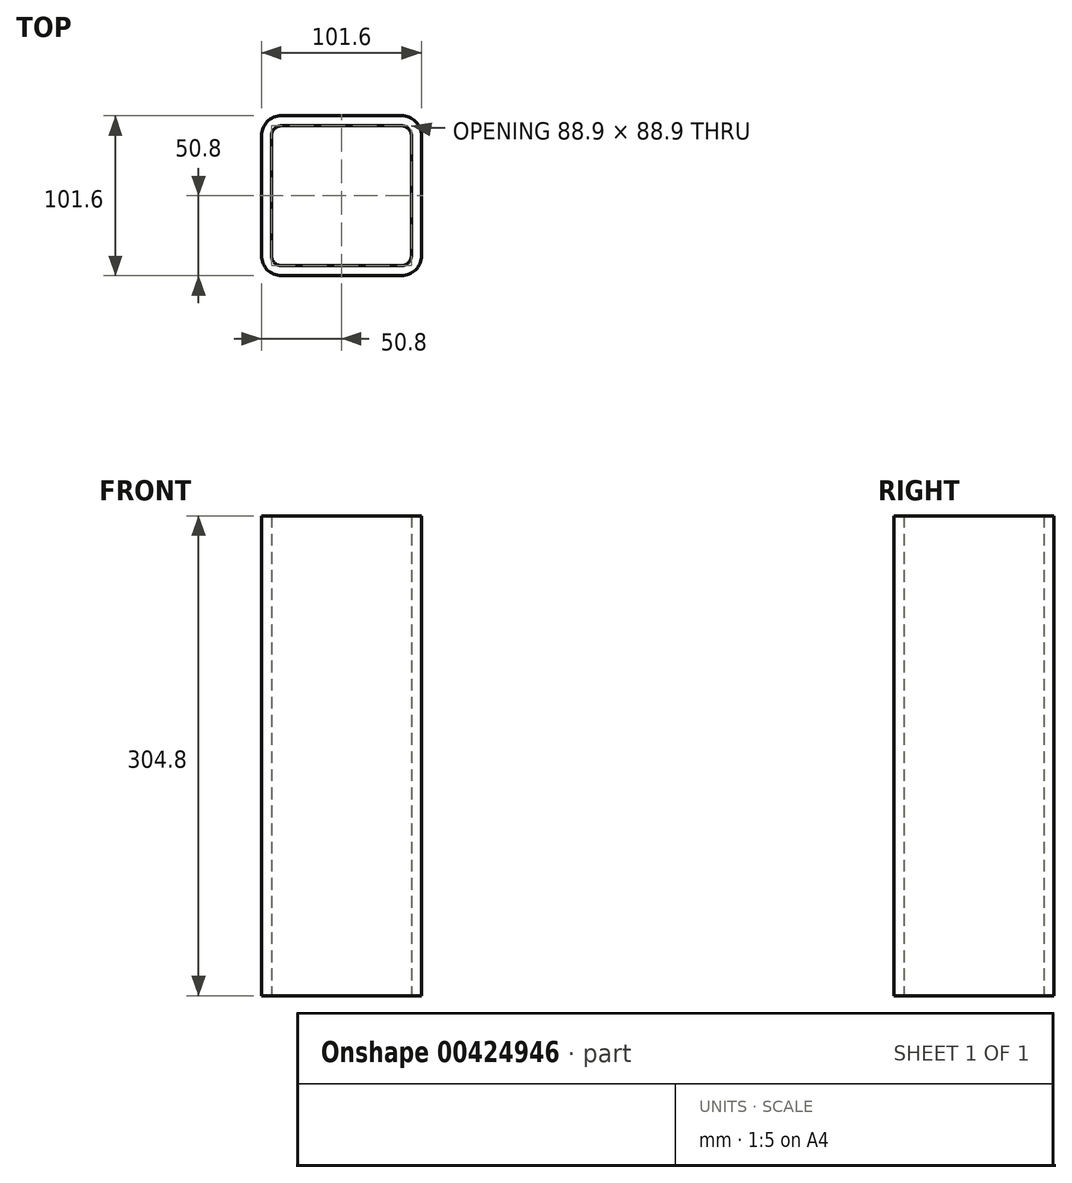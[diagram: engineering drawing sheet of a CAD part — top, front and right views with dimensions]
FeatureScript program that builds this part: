
annotation { "Feature Type Name" : "Feature", "Feature Type Description" : "" }
export const myFeature = defineFeature(function(context is Context, id is Id, definition is map)
    precondition{}
    {
        {
            var Q0;
            Q0=qCreatedBy(makeId("Top.planeOp"),FACE);
            var sketch = newSketch(context, id + "F0", { "sketchPlane" : qUnion([Q0])});
            skLineSegment(sketch, "E0.bottom", {"start": v(38.1, -50.8) * mm, "end": v(-38.1, -50.8) * mm});
            skLineSegment(sketch, "E0.top", {"start": v(38.1, 50.8) * mm, "end": v(-38.1, 50.8) * mm});
            skLineSegment(sketch, "E0.left", {"start": v(50.8, -38.1) * mm, "end": v(50.8, 38.1) * mm});
            skLineSegment(sketch, "E0.right", {"start": v(-50.8, -38.1) * mm, "end": v(-50.8, 38.1) * mm});
            skPoint(sketch, "E0.middle", {"position": v(0, 0) * mm});
            skPoint(sketch, "E1.visualSharp", {"position": v(-50.8, 50.8) * mm});
            skArc(sketch, "E1.filletArc", {"start": v(-38.1, 50.8) * mm, "mid": v(-47.08, 47.08) * mm, "end": v(-50.8, 38.1) * mm});
            skPoint(sketch, "E2.visualSharp", {"position": v(50.8, 50.8) * mm});
            skArc(sketch, "E2.filletArc", {"start": v(50.8, 38.1) * mm, "mid": v(47.08, 47.08) * mm, "end": v(38.1, 50.8) * mm});
            skPoint(sketch, "E3.visualSharp", {"position": v(50.8, -50.8) * mm});
            skArc(sketch, "E3.filletArc", {"start": v(38.1, -50.8) * mm, "mid": v(47.08, -47.08) * mm, "end": v(50.8, -38.1) * mm});
            skPoint(sketch, "E4.visualSharp", {"position": v(-50.8, -50.8) * mm});
            skArc(sketch, "E4.filletArc", {"start": v(-50.8, -38.1) * mm, "mid": v(-47.08, -47.08) * mm, "end": v(-38.1, -50.8) * mm});
            skArc(sketch, "E5.0", {"start": v(44.45, 38.1) * mm, "mid": v(42.6, 42.6) * mm, "end": v(38.1, 44.45) * mm});
            skLineSegment(sketch, "E5.1", {"start": v(44.45, -38.1) * mm, "end": v(44.45, 38.1) * mm});
            skLineSegment(sketch, "E5.2", {"start": v(38.1, 44.45) * mm, "end": v(-38.1, 44.45) * mm});
            skArc(sketch, "E5.3", {"start": v(38.1, -44.45) * mm, "mid": v(42.6, -42.6) * mm, "end": v(44.45, -38.1) * mm});
            skArc(sketch, "E5.4", {"start": v(-38.1, 44.45) * mm, "mid": v(-42.6, 42.6) * mm, "end": v(-44.45, 38.1) * mm});
            skLineSegment(sketch, "E5.5", {"start": v(-44.45, -38.1) * mm, "end": v(-44.45, 38.1) * mm});
            skArc(sketch, "E5.6", {"start": v(-44.45, -38.1) * mm, "mid": v(-42.6, -42.6) * mm, "end": v(-38.1, -44.45) * mm});
            skLineSegment(sketch, "E5.7", {"start": v(38.1, -44.45) * mm, "end": v(-38.1, -44.45) * mm});
            skSolve(sketch);
        }
        {
            var Q0;
            Q0=makeQuery(id+"F0.imprint","IMPRINT",FACE,{"disambiguationData":[TD([[makeQuery(id+"F0.imprint","IMPRINT",EDGE,{"derivedFrom":sQuery(id+"F0.wireOp",EDGE,"E0.bottom")}),-1.0]])]});
            extrude(context, id + "F1", {"entities" : qUnion([Q0]), "depth" : 304.8 * mm, "symmetric" : true});
        }
    });
